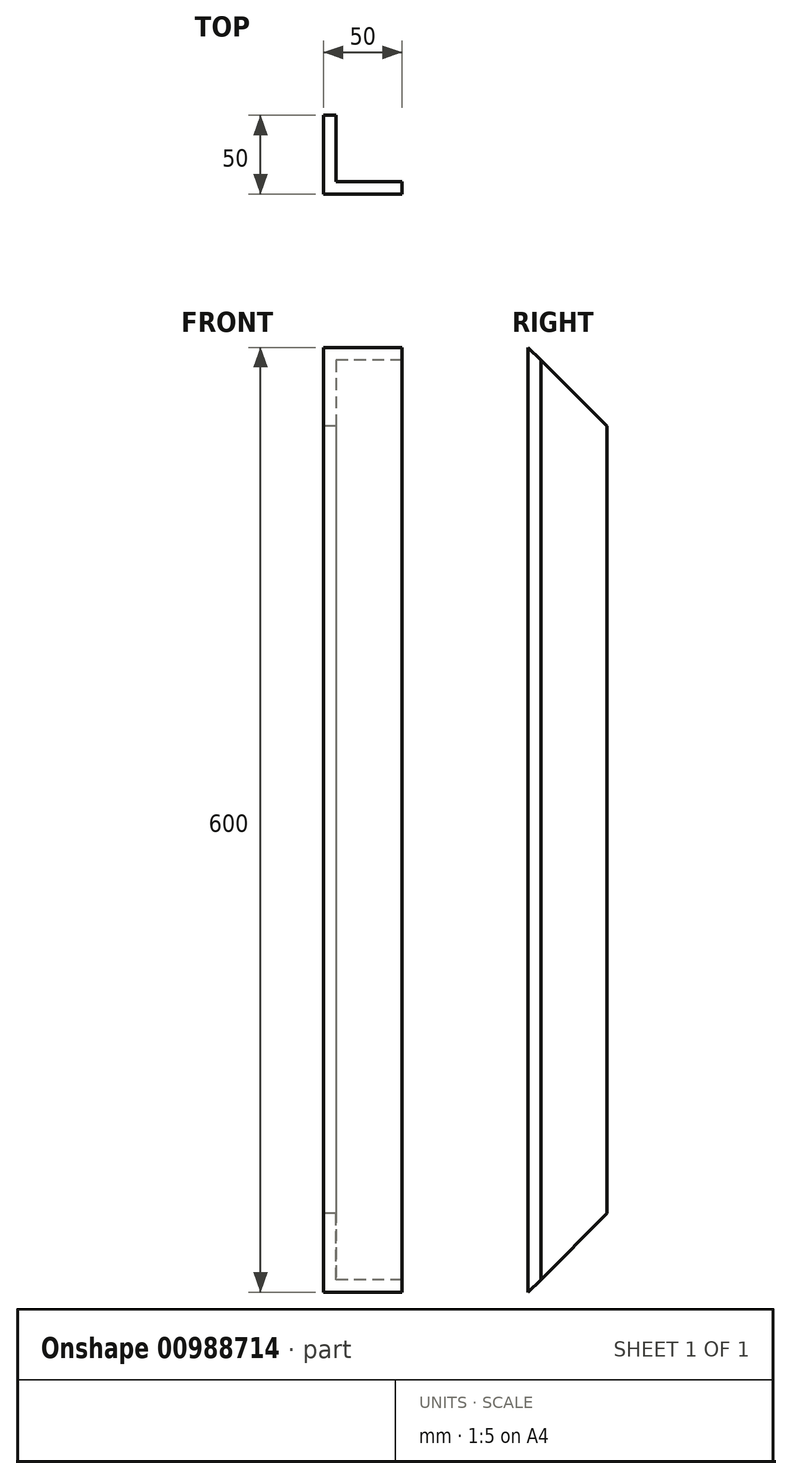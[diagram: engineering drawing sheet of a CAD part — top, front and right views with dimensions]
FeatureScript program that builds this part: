
annotation { "Feature Type Name" : "Feature", "Feature Type Description" : "" }
export const myFeature = defineFeature(function(context is Context, id is Id, definition is map)
    precondition{}
    {
        {
            var Q0;
            Q0=qCreatedBy(makeId("Top.planeOp"),FACE);
            var sketch = newSketch(context, id + "F0", { "sketchPlane" : qUnion([Q0])});
            skLineSegment(sketch, "E0", {"start": v(0, 0) * mm, "end": v(0, 50) * mm});
            skLineSegment(sketch, "E1", {"start": v(0, 50) * mm, "end": v(8, 50) * mm});
            skLineSegment(sketch, "E2", {"start": v(8, 50) * mm, "end": v(8, 8) * mm});
            skLineSegment(sketch, "E3", {"start": v(8, 8) * mm, "end": v(50, 8) * mm});
            skLineSegment(sketch, "E4", {"start": v(50, 8) * mm, "end": v(50, 0) * mm});
            skLineSegment(sketch, "E5", {"start": v(50, 0) * mm, "end": v(0, 0) * mm});
            skSolve(sketch);
        }
        {
            var Q0;
            Q0=qSketchRegion(id+"F0",true);
            extrude(context, id + "F1", {"entities" : qUnion([Q0]), "depth" : 600 * mm, "offsetDistance" : 25 * mm});
        }
        {
            var Q0;
            Q0=makeQuery(id+"F1.opExtrude","SWEPT_FACE",FACE,{"disambiguationData":[OSD([sQuery(id+"F0.wireOp",EDGE,"E0")])]});
            var sketch = newSketch(context, id + "F2", { "sketchPlane" : qUnion([Q0])});
            skLineSegment(sketch, "E6", {"start": v(0, 600) * mm, "end": v(0, 550) * mm});
            skLineSegment(sketch, "E7", {"start": v(0, 550) * mm, "end": v(-50, 550) * mm});
            skLineSegment(sketch, "E8", {"start": v(-50, 550) * mm, "end": v(0, 600) * mm});
            skSolve(sketch);
        }
        {
            var Q0;
            {var subQ0=sQuery(id+"F2.wireOp",EDGE,"E8");Q0=makeQuery(id+"F2.imprint","IMPRINT",FACE,{"disambiguationData":[TD([[makeQuery(id+"F2.imprint","IMPRINT",EDGE,{"derivedFrom":subQ0}),1.0]])]});}
            var Q1;
            Q1=makeQuery(id+"F1.opExtrude","SWEPT_FACE",FACE,{"disambiguationData":[OSD([sQuery(id+"F0.wireOp",EDGE,"E2")])]});
            extrude(context, id + "F3", {"entities" : qUnion([Q0]), "operationType" : NewBodyOperationType.REMOVE, "endBound" : BoundingType.THROUGH_ALL, "oppositeDirection" : true, "depth" : 25 * mm, "endBoundEntityFace" : qUnion([Q1]), "offsetDistance" : 25 * mm});
        }
        {
            var Q0;
            Q0=makeQuery(id+"F1.opExtrude","SWEPT_FACE",FACE,{"disambiguationData":[OSD([sQuery(id+"F0.wireOp",EDGE,"E0")])]});
            var sketch = newSketch(context, id + "F4", { "sketchPlane" : qUnion([Q0])});
            skLineSegment(sketch, "E9", {"start": v(0, 0) * mm, "end": v(-50, 0) * mm});
            skLineSegment(sketch, "E10", {"start": v(-50, 0) * mm, "end": v(-50, 50) * mm});
            skLineSegment(sketch, "E11", {"start": v(-50, 50) * mm, "end": v(0, 0) * mm});
            skSolve(sketch);
        }
        {
            var Q0;
            {var subQ3=sQuery(id+"F4.wireOp",EDGE,"E10");Q0=makeQuery(id+"F4.imprint","IMPRINT",FACE,{"disambiguationData":[TD([[makeQuery(id+"F4.imprint","IMPRINT",EDGE,{"derivedFrom":subQ3}),1.0]])]});}
            var Q1;
            Q1=makeQuery(id+"F1.opExtrude","SWEPT_FACE",FACE,{"disambiguationData":[OSD([sQuery(id+"F0.wireOp",EDGE,"E2")])]});
            extrude(context, id + "F5", {"entities" : qUnion([Q0]), "operationType" : NewBodyOperationType.REMOVE, "endBound" : BoundingType.THROUGH_ALL, "oppositeDirection" : true, "depth" : 25 * mm, "endBoundEntityFace" : qUnion([Q1]), "offsetDistance" : 25 * mm});
        }
    });
